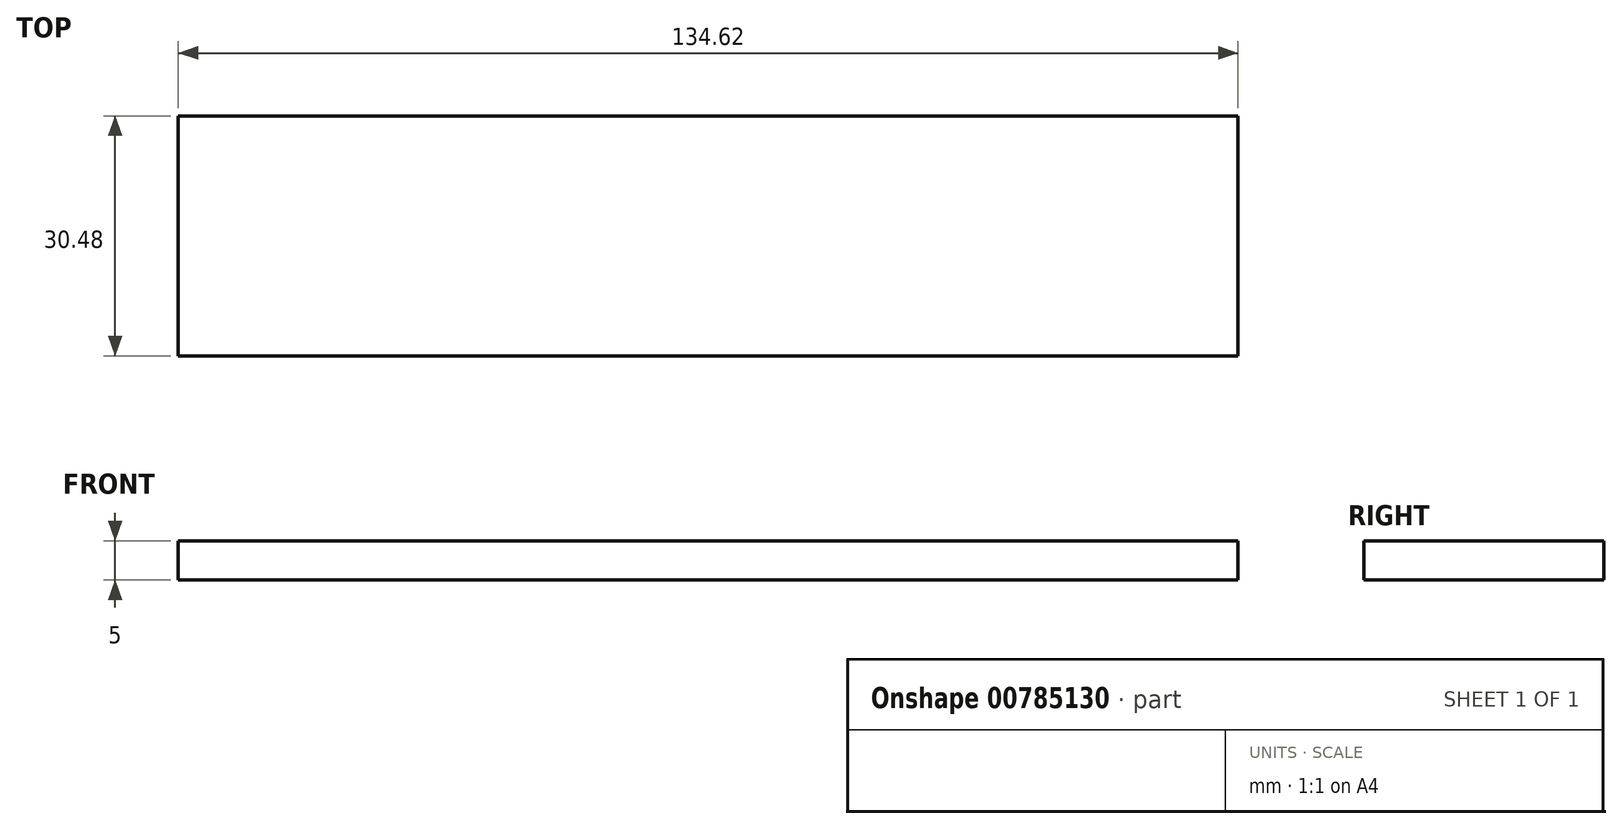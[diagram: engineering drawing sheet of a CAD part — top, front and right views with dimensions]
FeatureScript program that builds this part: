
annotation { "Feature Type Name" : "Feature", "Feature Type Description" : "" }
export const myFeature = defineFeature(function(context is Context, id is Id, definition is map)
    precondition{}
    {
        {
            var Q0;
            Q0=qCreatedBy(makeId("Top.planeOp"),FACE);
            var sketch = newSketch(context, id + "F0", { "sketchPlane" : qUnion([Q0])});
            skPoint(sketch, "E0.middle", {"position": v(0, 0) * mm});
            skLineSegment(sketch, "E1.bottom", {"start": v(-67.31, 15.24) * mm, "end": v(67.31, 15.24) * mm});
            skLineSegment(sketch, "E1.top", {"start": v(-67.31, -15.24) * mm, "end": v(67.31, -15.24) * mm});
            skLineSegment(sketch, "E1.left", {"start": v(-67.31, 15.24) * mm, "end": v(-67.31, -15.24) * mm});
            skLineSegment(sketch, "E1.right", {"start": v(67.31, 15.24) * mm, "end": v(67.31, -15.24) * mm});
            skSolve(sketch);
        }
        {
            var Q0;
            Q0=makeQuery(id+"F0.imprint","IMPRINT",FACE,{"disambiguationData":[TD([[makeQuery(id+"F0.imprint","IMPRINT",EDGE,{"derivedFrom":sQuery(id+"F0.wireOp",EDGE,"E1.bottom")}),-1.0]])]});
            extrude(context, id + "F1", {"entities" : qUnion([Q0]), "depth" : 5 * mm, "offsetDistance" : 25.4 * mm});
        }
    });
